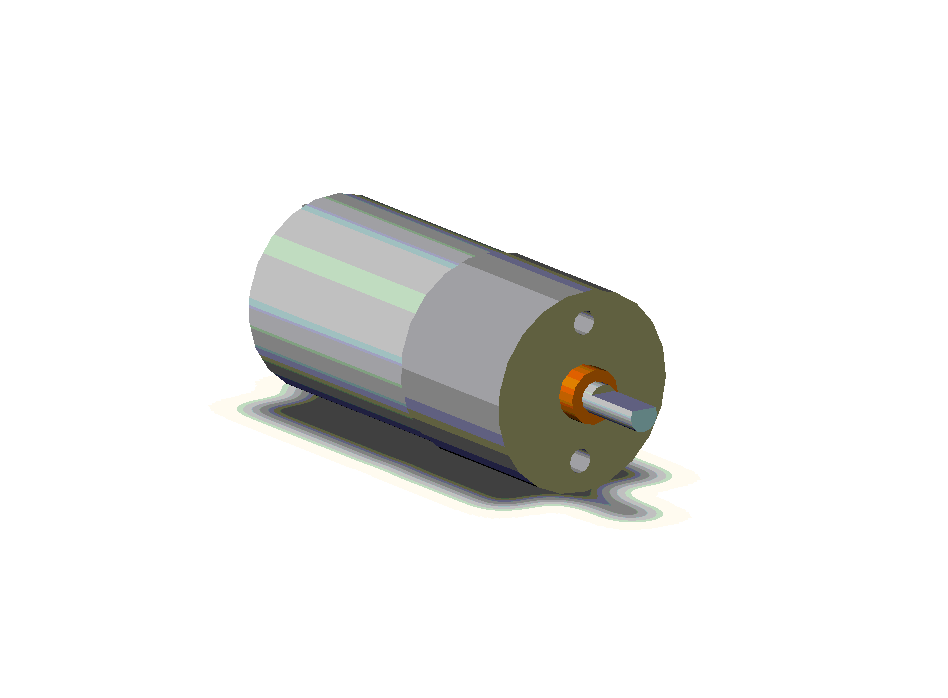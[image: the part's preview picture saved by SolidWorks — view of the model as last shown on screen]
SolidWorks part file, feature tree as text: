
SOLIDWORKS PART (.sldprt)
format: sldprt  version: not decoded by parser v0  size: 363,520 bytes
history: native  units: mm
features: sketch x9, extrude x6, cut_extrude x3, fillet x2 (+8 scaffold rows collapsed)
feature tree (28):
  scaffold x8  (default folders/planes/origin — collapsed)
  sketch  "Sketch2"  dims[D1=24.8mm]
  extrude  "Base-Extrude"  Depth=19.05mm
  sketch  "Sketch3"  dims[D1=6.83mm]
  extrude  "Boss-Extrude1"  Depth=2.54mm
  sketch  "Sketch5"  dims[D1=3.88mm]
  extrude  "Boss-Extrude2"  Depth=9.55mm
  sketch  "Sketch6"  dims[D2=2.5mm D1=~0.894972mm]
  cut_extrude  "Cut-Extrude1"  Depth=8mm
  sketch  "Sketch7"  dims[D1=24.0mm]
  extrude  "Boss-Extrude3"  Depth=30.25mm
  sketch  "Sketch8"  dims[D2=8.38mm D1=3.2mm]
  extrude  "Boss-Extrude4"  Depth=2mm
  sketch  "Sketch9"  dims[D1=19.05mm D2=0.21mm D3=0.21mm D4=9.525mm D5=2.8mm D6=1.4mm D7=1.4mm D8=2.8mm]
  extrude  "Boss-Extrude5"  Depth=5mm
  fillet  "Fillet1"  Radius=1.4mm
  fillet  "Fillet2"  Radius=1.4mm
  sketch  "Sketch10"  dims[D1=0.8mm]
  cut_extrude  "Cut-Extrude2"  [1 undecoded]
  sketch  "Sketch11"  dims[D3=3.0mm D4=3.0mm D1=8.5mm D2=8.5mm]
  cut_extrude  "Cut-Extrude3"  Depth=4mm
decode coverage: 19 of 20 modeling features carry decoded parameters
note: ~ marks probable driven/reference dimensions
note: 1 parameter value undecoded
note: suppression state not decoded; provenance and decode notes live in map.json
